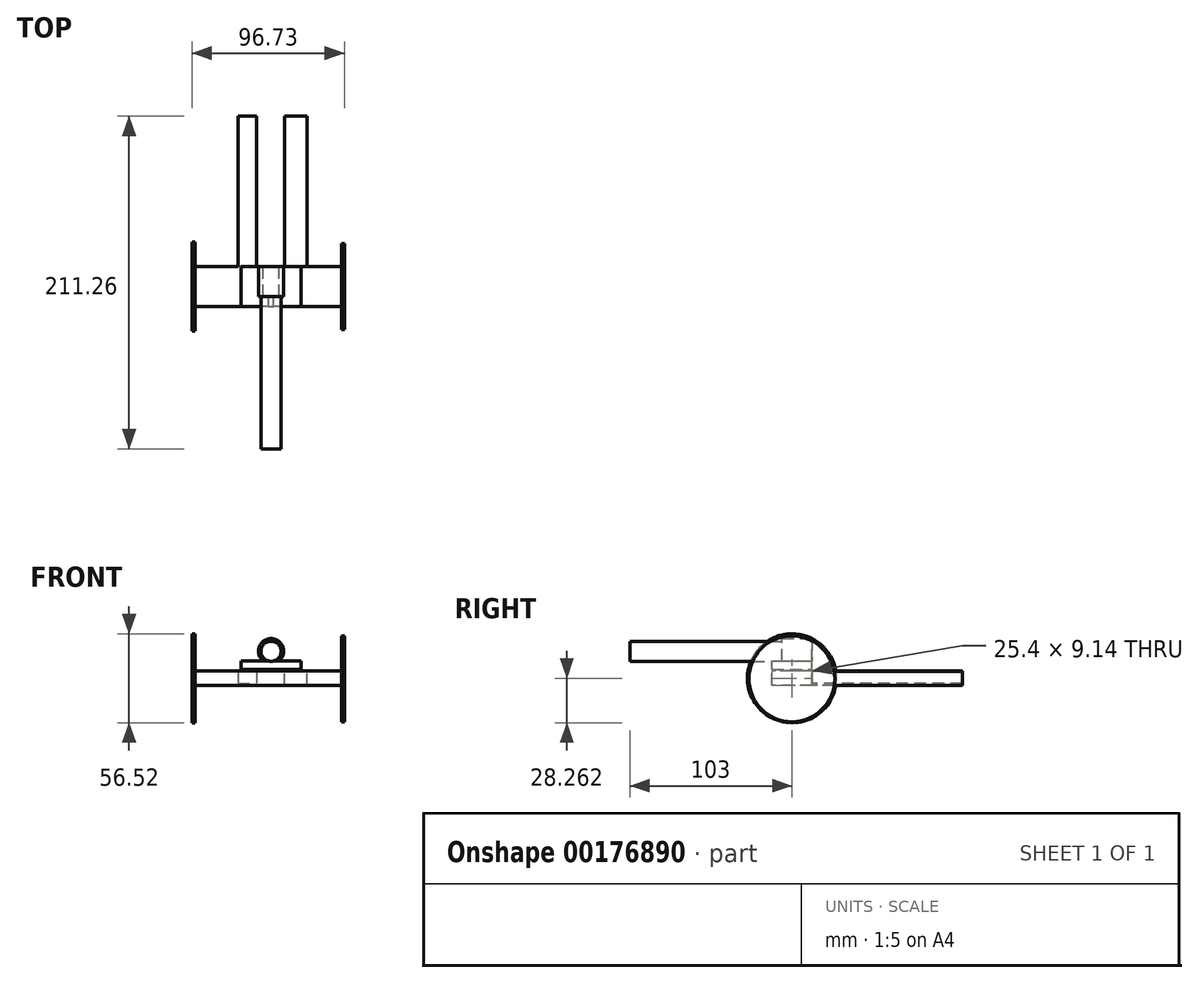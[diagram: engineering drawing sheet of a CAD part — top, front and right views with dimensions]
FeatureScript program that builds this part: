
annotation { "Feature Type Name" : "Feature", "Feature Type Description" : "" }
export const myFeature = defineFeature(function(context is Context, id is Id, definition is map)
    precondition{}
    {
        {
            var Q0;
            Q0=qCreatedBy(makeId("Front.planeOp"),FACE);
            var sketch = newSketch(context, id + "F0", { "sketchPlane" : qUnion([Q0])});
            skCircle(sketch, "E0", {"center": v(0, 0) * mm, "radius": 6.4 * mm});
            skSolve(sketch);
        }
        {
            var Q0;
            Q0=makeQuery(id+"F0.imprint","IMPRINT",FACE,{"disambiguationData":[TD([[makeQuery(id+"F0.imprint","IMPRINT",EDGE,{"derivedFrom":sQuery(id+"F0.wireOp",EDGE,"E0")}),1.0]])]});
            extrude(context, id + "F1", {"entities" : qUnion([Q0]), "depth" : 115.7 * mm});
        }
        {
            var Q0;
            Q0=qCreatedBy(makeId("Front.planeOp"),FACE);
            var sketch = newSketch(context, id + "F2", { "sketchPlane" : qUnion([Q0])});
            skLineSegment(sketch, "E1.bottom", {"start": v(19.2, -11.65) * mm, "end": v(-19.2, -11.65) * mm});
            skLineSegment(sketch, "E1.top", {"start": v(19.2, -6.17) * mm, "end": v(-19.2, -6.17) * mm});
            skLineSegment(sketch, "E1.left", {"start": v(19.2, -11.65) * mm, "end": v(19.2, -6.17) * mm});
            skLineSegment(sketch, "E1.right", {"start": v(-19.2, -11.65) * mm, "end": v(-19.2, -6.17) * mm});
            skPoint(sketch, "E1.middle", {"position": v(0, -8.91) * mm});
            skSolve(sketch);
        }
        {
            var Q0;
            Q0 = qSketchRegion(id + "F2", true);
            extrude(context, id + "F3", {"entities" : qUnion([Q0]), "operationType" : NewBodyOperationType.ADD, "depth" : 25.4 * mm});
        }
        {
            var Q0;
            Q0=qCreatedBy(makeId("Front.planeOp"),FACE);
            var sketch = newSketch(context, id + "F4", { "sketchPlane" : qUnion([Q0])});
            skCircle(sketch, "E2", {"center": v(0, 0) * mm, "radius": 8.04 * mm});
            skSolve(sketch);
        }
        {
            var Q0;
            Q0=makeQuery(id+"F4.imprint","IMPRINT",FACE,{"disambiguationData":[TD([[makeQuery(id+"F4.imprint","IMPRINT",EDGE,{"derivedFrom":sQuery(id+"F4.wireOp",EDGE,"E2")}),1.0]])]});
            extrude(context, id + "F5", {"entities" : qUnion([Q0]), "operationType" : NewBodyOperationType.ADD, "depth" : 19.02 * mm});
        }
        {
            var Q0;
            Q0=qCreatedBy(makeId("Front.planeOp"),FACE);
            var sketch = newSketch(context, id + "F6", { "sketchPlane" : qUnion([Q0])});
            skLineSegment(sketch, "E3.bottom", {"start": v(46.62, -21.7) * mm, "end": v(-46.62, -21.7) * mm});
            skLineSegment(sketch, "E3.top", {"start": v(46.62, -12.57) * mm, "end": v(-46.62, -12.57) * mm});
            skLineSegment(sketch, "E3.left", {"start": v(46.62, -21.7) * mm, "end": v(46.62, -12.57) * mm});
            skLineSegment(sketch, "E3.right", {"start": v(-46.62, -21.7) * mm, "end": v(-46.62, -12.57) * mm});
            skPoint(sketch, "E3.middle", {"position": v(0, -17.14) * mm});
            skSolve(sketch);
        }
        {
            var Q0;
            Q0 = qSketchRegion(id + "F6", true);
            extrude(context, id + "F7", {"entities" : qUnion([Q0]), "depth" : 25.4 * mm});
        }
        {
            var Q0;
            Q0=makeQuery(id+"F7.opExtrude","SWEPT_FACE",FACE,{"disambiguationData":[OSD([sQuery(id+"F6.wireOp",EDGE,"E3.left")])]});
            var sketch = newSketch(context, id + "F8", { "sketchPlane" : qUnion([Q0])});
            skCircle(sketch, "E4", {"center": v(-12.75, -17.48) * mm, "radius": 27.26 * mm});
            skSolve(sketch);
        }
        {
            var Q0;
            Q0 = qSketchRegion(id + "F8", true);
            var Q1;
            Q1=makeQuery(id+"F7.opExtrude","SWEPT_FACE",FACE,{"disambiguationData":[OSD([sQuery(id+"F6.wireOp",EDGE,"E3.right")])]});
            extrude(context, id + "F9", {"entities" : qUnion([Q0, Q1]), "operationType" : NewBodyOperationType.ADD, "oppositeDirection" : true, "depth" : 1.74 * mm});
        }
        {
            var Q0;
            Q0=makeQuery(id+"F9.opExtrude","CAP_FACE",FACE,{"disambiguationData":[OSD([sQuery(id+"F6.wireOp",EDGE,"E3.right")])],"isStart":false});
            var sketch = newSketch(context, id + "F10", { "sketchPlane" : qUnion([Q0])});
            skCircle(sketch, "E5", {"center": v(12.7, -17.14) * mm, "radius": 28.26 * mm});
            skPoint(sketch, "E5.centerSnap0", {"position": v(12.7, -12.57) * mm});
            skPoint(sketch, "E5.centerSnap1", {"position": v(25.4, -17.14) * mm});
            skSolve(sketch);
        }
        {
            var Q0;
            Q0 = qSketchRegion(id + "F10", true);
            extrude(context, id + "F11", {"entities" : qUnion([Q0]), "operationType" : NewBodyOperationType.ADD, "depth" : 1.76 * mm});
        }
        {
            var Q0;
            {var subQ0=sQuery(id+"F6.wireOp",EDGE,"E3.right");Q0=makeQuery(id+"F9.boolean.opBoolean","MERGE",FACE,{"derivedFrom":[makeQuery(id+"F7.opExtrude","CAP_FACE",FACE,{"disambiguationData":[OSD([sQuery(id+"F6.wireOp",EDGE,"E3.bottom"),sQuery(id+"F6.wireOp",EDGE,"E3.top"),sQuery(id+"F6.wireOp",EDGE,"E3.left"),subQ0])],"isStart":true}),makeQuery(id+"F9.opExtrude","SWEPT_FACE",FACE,{"disambiguationData":[OSD([subQ0]),TDD([makeQuery(id+"F7.opExtrude","CAP_EDGE",EDGE,{"disambiguationData":[OSD([subQ0])],"isStart":true})])]})]});}
            var sketch = newSketch(context, id + "F12", { "sketchPlane" : qUnion([Q0])});
            skLineSegment(sketch, "E6.bottom", {"start": v(-8.48, -21.7) * mm, "end": v(-22.77, -21.7) * mm});
            skLineSegment(sketch, "E6.top", {"start": v(-8.48, -12.94) * mm, "end": v(-22.77, -12.94) * mm});
            skLineSegment(sketch, "E6.left", {"start": v(-8.48, -21.7) * mm, "end": v(-8.48, -12.94) * mm});
            skLineSegment(sketch, "E6.right", {"start": v(-22.77, -21.7) * mm, "end": v(-22.77, -12.94) * mm});
            skPoint(sketch, "E6.middle", {"position": v(-15.62, -17.32) * mm});
            skLineSegment(sketch, "E7.bottom", {"start": v(20.99, -12.57) * mm, "end": v(9.1, -12.57) * mm});
            skLineSegment(sketch, "E7.top", {"start": v(20.99, -20.54) * mm, "end": v(9.1, -20.54) * mm});
            skLineSegment(sketch, "E7.left", {"start": v(20.99, -12.57) * mm, "end": v(20.99, -20.54) * mm});
            skLineSegment(sketch, "E7.right", {"start": v(9.1, -12.57) * mm, "end": v(9.1, -20.54) * mm});
            skPoint(sketch, "E7.middle", {"position": v(15.04, -16.56) * mm});
            skSolve(sketch);
        }
        {
            var Q0;
            Q0=makeQuery(id+"F12.imprint","IMPRINT",FACE,{"disambiguationData":[TD([[makeQuery(id+"F12.imprint","IMPRINT",EDGE,{"derivedFrom":sQuery(id+"F12.wireOp",EDGE,"E7.bottom")}),-1.0]])]});
            var Q1;
            Q1=makeQuery(id+"F12.imprint","IMPRINT",FACE,{"disambiguationData":[TD([[makeQuery(id+"F12.imprint","IMPRINT",EDGE,{"derivedFrom":sQuery(id+"F12.wireOp",EDGE,"E6.bottom")}),1.0]])]});
            extrude(context, id + "F13", {"entities" : qUnion([Q0, Q1]), "operationType" : NewBodyOperationType.ADD, "depth" : 95.56 * mm});
        }
    });
